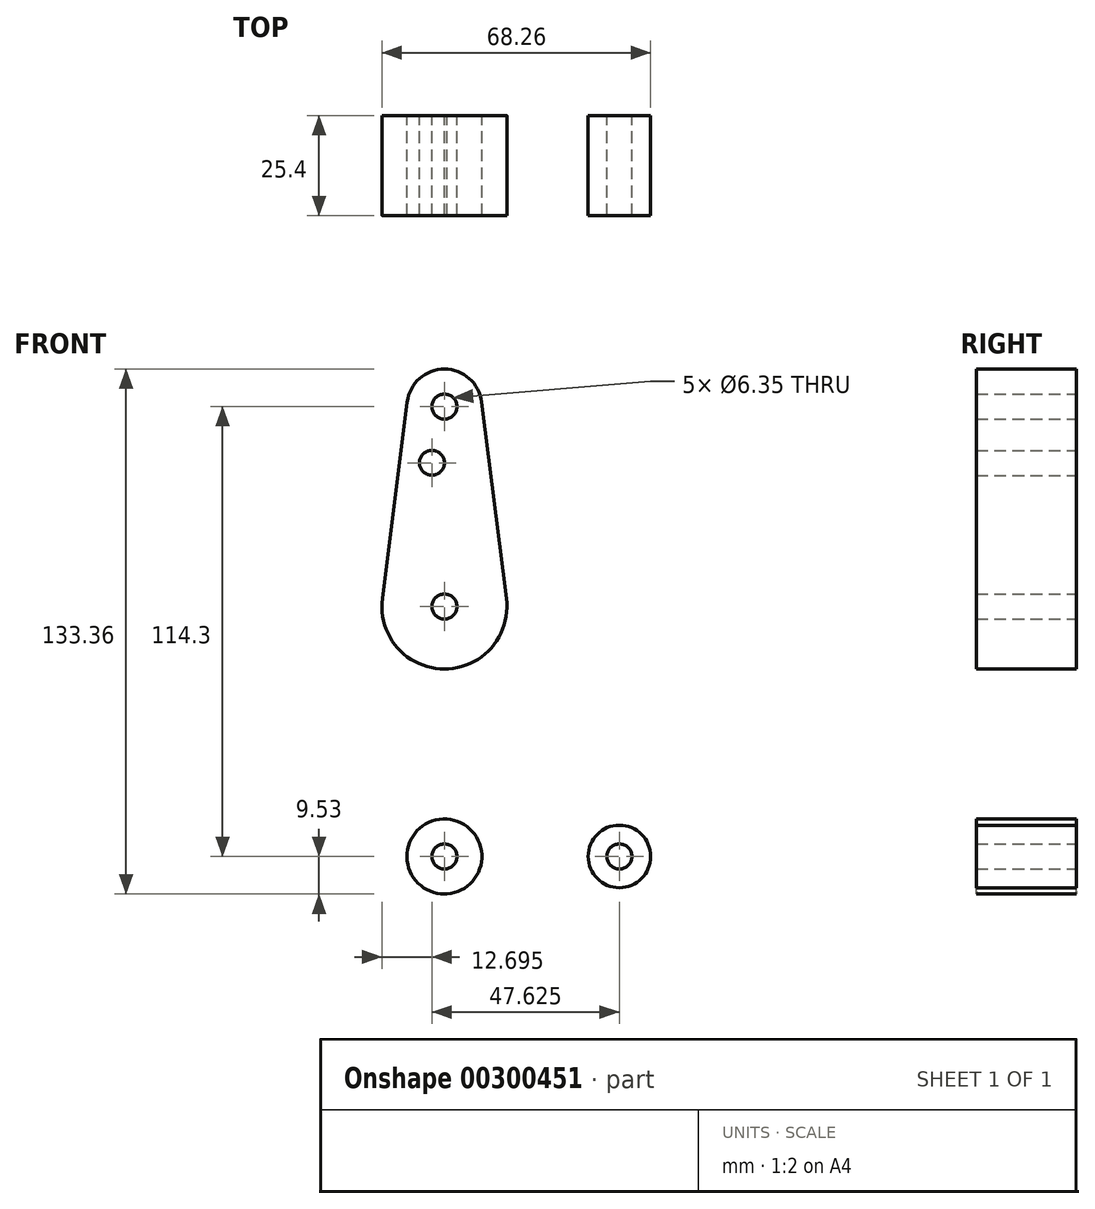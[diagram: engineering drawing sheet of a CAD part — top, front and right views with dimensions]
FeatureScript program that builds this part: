
annotation { "Feature Type Name" : "Feature", "Feature Type Description" : "" }
export const myFeature = defineFeature(function(context is Context, id is Id, definition is map)
    precondition{}
    {
        {
            var Q0;
            Q0=qCreatedBy(makeId("Front.planeOp"),FACE);
            var sketch = newSketch(context, id + "F0", { "sketchPlane" : qUnion([Q0])});
            skCircle(sketch, "E0", {"center": v(0, 0) * mm, "radius": 9.53 * mm});
            skCircle(sketch, "E1", {"center": v(44.45, 0) * mm, "radius": 7.94 * mm});
            skCircle(sketch, "E2", {"center": v(0, 63.5) * mm, "radius": 15.88 * mm});
            skCircle(sketch, "E3", {"center": v(0, 114.3) * mm, "radius": 9.53 * mm});
            skLineSegment(sketch, "E4", {"start": v(0, 114.3) * mm, "end": v(0, 0) * mm, "construction": true});
            skLineSegment(sketch, "E5", {"start": v(0, 0) * mm, "end": v(44.45, 0) * mm, "construction": true});
            skLineSegment(sketch, "E6", {"start": v(9.45, 115.5) * mm, "end": v(15.75, 65.48) * mm});
            skLineSegment(sketch, "E7", {"start": v(-9.45, 115.5) * mm, "end": v(-15.75, 65.48) * mm});
            skLineSegment(sketch, "E8", {"start": v(18.93, 8.85) * mm, "end": v(44.73, 7.93) * mm});
            skLineSegment(sketch, "E9", {"start": v(0, -9.53) * mm, "end": v(44.73, -7.93) * mm});
            skLineSegment(sketch, "E10", {"start": v(-15.8, 61.91) * mm, "end": v(-9.57, 0) * mm});
            skLineSegment(sketch, "E11", {"start": v(11.3, 17.6) * mm, "end": v(15.75, 61.52) * mm});
            skCircle(sketch, "E12", {"center": v(0, 114.3) * mm, "radius": 3.18 * mm});
            skCircle(sketch, "E13", {"center": v(0, 63.5) * mm, "radius": 3.18 * mm});
            skCircle(sketch, "E14", {"center": v(0, 0) * mm, "radius": 3.18 * mm});
            skCircle(sketch, "E15", {"center": v(44.45, 0) * mm, "radius": 3.18 * mm});
            skCircle(sketch, "E16", {"center": v(-3.17, 100.03) * mm, "radius": 3.18 * mm});
            skPoint(sketch, "E17.newPointB", {"position": v(0, 9.53) * mm});
            skArc(sketch, "E17.filletArc", {"start": v(11.3, 17.6) * mm, "mid": v(13.22, 11.57) * mm, "end": v(18.93, 8.85) * mm});
            skSolve(sketch);
        }
        {
            var Q0;
            {var subQ0=sQuery(id+"F0.wireOp",EDGE,"E9");var subQ1=sQuery(id+"F0.wireOp",EDGE,"E0");var subQ2=makeQuery(id+"F0.imprint","INTERSECT",VERTEX,{"disambiguationData":[OD(0.0)],"derivedFrom":[subQ1,subQ0]});Q0=makeQuery(id+"F0.imprint","IMPRINT",FACE,{"disambiguationData":[TD([[makeQuery(id+"F0.imprint","IMPRINT",EDGE,{"disambiguationData":[TD([[subQ2,-1.0]])],"derivedFrom":subQ1}),1.0]])]});}
            var Q1;
            Q1=makeQuery(id+"F0.imprint","IMPRINT",FACE,{"disambiguationData":[TD([[makeQuery(id+"F0.imprint","IMPRINT",EDGE,{"derivedFrom":sQuery(id+"F0.wireOp",EDGE,"E15")}),-1.0]])]});
            var Q2;
            Q2=makeQuery(id+"F0.imprint","IMPRINT",FACE,{"disambiguationData":[TD([[makeQuery(id+"F0.imprint","IMPRINT",EDGE,{"derivedFrom":sQuery(id+"F0.wireOp",EDGE,"E13")}),-1.0]])]});
            var Q3;
            {var subQ1=sQuery(id+"F0.wireOp",EDGE,"E6");Q3=makeQuery(id+"F0.imprint","IMPRINT",FACE,{"disambiguationData":[TD([[makeQuery(id+"F0.imprint","IMPRINT",EDGE,{"derivedFrom":subQ1}),-1.0]])]});}
            var Q4;
            Q4=makeQuery(id+"F0.imprint","IMPRINT",FACE,{"disambiguationData":[TD([[makeQuery(id+"F0.imprint","IMPRINT",EDGE,{"derivedFrom":sQuery(id+"F0.wireOp",EDGE,"E12")}),-1.0]])]});
            var Q5;
            Q5=makeQuery(id+"F0.imprint","IMPRINT",FACE,{"disambiguationData":[TD([[makeQuery(id+"F0.imprint","IMPRINT",EDGE,{"derivedFrom":sQuery(id+"F0.wireOp",EDGE,"E14")}),-1.0]])]});
            extrude(context, id + "F1", {"entities" : qUnion([Q0, Q1, Q2, Q3, Q4, Q5]), "depth" : 25.4 * mm});
        }
    });
